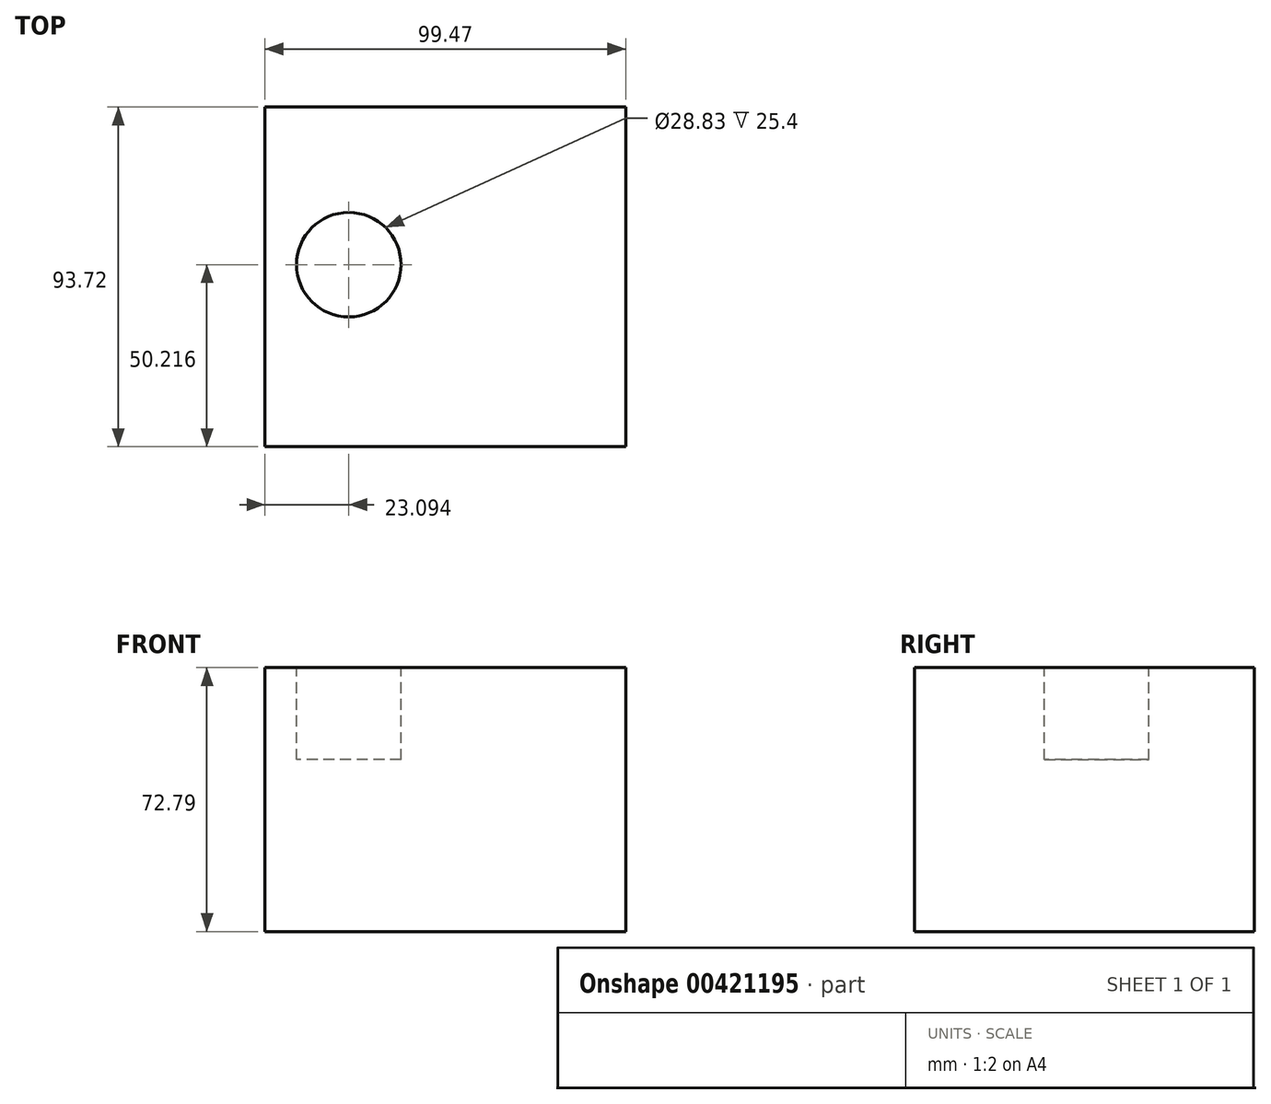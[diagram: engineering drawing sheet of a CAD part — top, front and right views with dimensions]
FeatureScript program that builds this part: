
annotation { "Feature Type Name" : "Feature", "Feature Type Description" : "" }
export const myFeature = defineFeature(function(context is Context, id is Id, definition is map)
    precondition{}
    {
        {
            var Q0;
            Q0=qCreatedBy(makeId("Front.planeOp"),FACE);
            var sketch = newSketch(context, id + "F0", { "sketchPlane" : qUnion([Q0])});
            skLineSegment(sketch, "E0.bottom", {"start": v(-62.42, 41.86) * mm, "end": v(37.05, 41.86) * mm});
            skLineSegment(sketch, "E0.top", {"start": v(-62.42, -30.92) * mm, "end": v(37.05, -30.92) * mm});
            skLineSegment(sketch, "E0.left", {"start": v(-62.42, 41.86) * mm, "end": v(-62.42, -30.92) * mm});
            skLineSegment(sketch, "E0.right", {"start": v(37.05, 41.86) * mm, "end": v(37.05, -30.92) * mm});
            skSolve(sketch);
        }
        {
            var Q0;
            Q0 = qSketchRegion(id + "F0", true);
            extrude(context, id + "F1", {"entities" : qUnion([Q0]), "depth" : 93.73 * mm});
        }
        {
            var Q0;
            Q0=makeQuery(id+"F1.opExtrude","SWEPT_FACE",FACE,{"disambiguationData":[OSD([sQuery(id+"F0.wireOp",EDGE,"E0.bottom")])]});
            var sketch = newSketch(context, id + "F2", { "sketchPlane" : qUnion([Q0])});
            skCircle(sketch, "E1", {"center": v(-39.33, -43.5) * mm, "radius": 14.42 * mm});
            skSolve(sketch);
        }
        {
            var Q0;
            Q0 = qSketchRegion(id + "F2", true);
            extrude(context, id + "F3", {"entities" : qUnion([Q0]), "operationType" : NewBodyOperationType.REMOVE, "oppositeDirection" : true, "depth" : 25.4 * mm});
        }
        {
            var Q0;
            Q0=makeQuery(id+"F1.opExtrude","SWEPT_BODY",BODY,{"disambiguationData":[OSD([sQuery(id+"F0.wireOp",EDGE,"E0.bottom"),sQuery(id+"F0.wireOp",EDGE,"E0.top"),sQuery(id+"F0.wireOp",EDGE,"E0.left"),sQuery(id+"F0.wireOp",EDGE,"E0.right")])]});
            transform(context, id + "F4", {"entities" : qUnion([Q0]), "transformType" : TransformType.TRANSLATION_3D, "dx" : 13.72 * mm, "dy" : -15 * mm, "dz" : 4.06 * mm, "makeCopy" : false});
        }
    });
